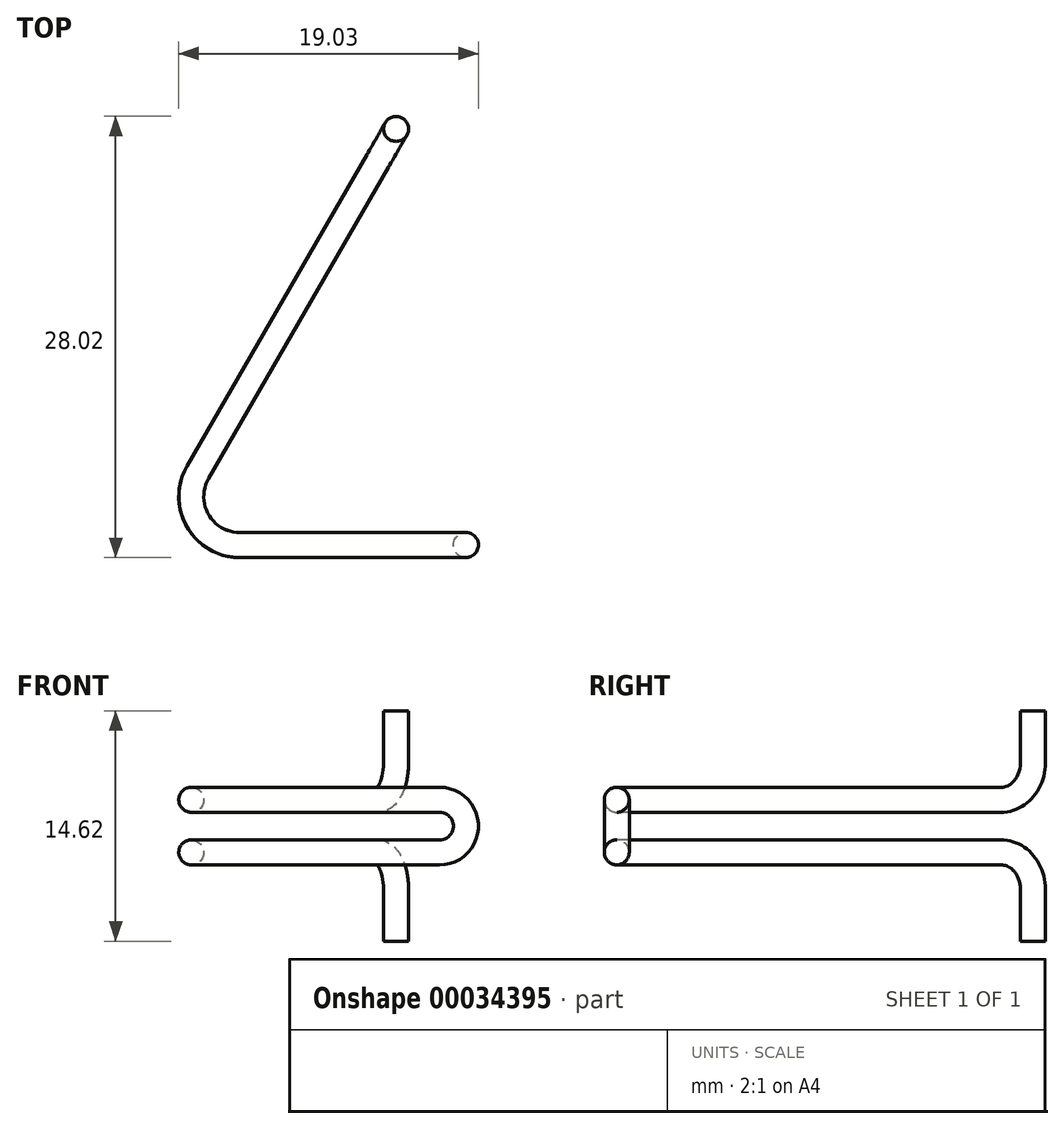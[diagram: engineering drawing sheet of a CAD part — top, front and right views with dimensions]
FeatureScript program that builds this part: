
annotation { "Feature Type Name" : "Feature", "Feature Type Description" : "" }
export const myFeature = defineFeature(function(context is Context, id is Id, definition is map)
    precondition{}
    {
        {
            var Q0;
            Q0=qCreatedBy(makeId("Top.planeOp"),FACE);
            var sketch = newSketch(context, id + "F0", { "sketchPlane" : qUnion([Q0])});
            skLineSegment(sketch, "E0", {"start": v(0, 0) * mm, "end": v(12.7, 0) * mm});
            skArc(sketch, "E1", {"start": v(-2.66, 4.61) * mm, "mid": v(-2.66, 1.54) * mm, "end": v(0, 0) * mm});
            skLineSegment(sketch, "E2", {"start": v(-2.66, 4.61) * mm, "end": v(8.77, 24.4) * mm});
            skSolve(sketch);
        }
        {
            var Q0;
            Q0=qCreatedBy(makeId("Right.planeOp"),FACE);
            var Q1;
            Q1=sQuery(id+"F0.wireOp",VERTEX,"E0.end");
            cPlane(context, id + "F1", {"entities" : qUnion([Q0, Q1]), "cplaneType" : CPlaneType.PLANE_POINT, "offset" : 152.4 * mm, "width" : 152.4 * mm, "height" : 152.4 * mm});
        }
        {
            var Q0;
            Q0=qCreatedBy(id+"F1.planeOp",FACE);
            var sketch = newSketch(context, id + "F2", { "sketchPlane" : qUnion([Q0])});
            skCircle(sketch, "E3", {"center": v(0, 0) * mm, "radius": 0.76 * mm});
            skSolve(sketch);
        }
        {
            var Q0;
            Q0=qCreatedBy(makeId("Front.planeOp"),FACE);
            var sketch = newSketch(context, id + "F3", { "sketchPlane" : qUnion([Q0])});
            skPoint(sketch, "E4.0", {"position": v(12.7, 0) * mm});
            skLineSegment(sketch, "E4.1", {"start": v(0, 0) * mm, "end": v(12.7, 0) * mm, "construction": true});
            skLineSegment(sketch, "E5", {"start": v(12.7, 0) * mm, "end": v(12.7, -3.34) * mm, "construction": true});
            skArc(sketch, "E6", {"start": v(12.7, -3.34) * mm, "mid": v(14.37, -1.67) * mm, "end": v(12.7, 0) * mm});
            skSolve(sketch);
        }
        {
            var Q0;
            Q0=qCreatedBy(makeId("Top.planeOp"),FACE);
            var Q1;
            Q1=sQuery(id+"F3.wireOp",VERTEX,"E6.start");
            cPlane(context, id + "F4", {"entities" : qUnion([Q0, Q1]), "cplaneType" : CPlaneType.PLANE_POINT, "offset" : 152.4 * mm, "width" : 152.4 * mm, "height" : 152.4 * mm});
        }
        {
            var Q0;
            Q0=qCreatedBy(id+"F4.planeOp",FACE);
            var sketch = newSketch(context, id + "F5", { "sketchPlane" : qUnion([Q0])});
            skLineSegment(sketch, "E7.0", {"start": v(0, 0) * mm, "end": v(12.7, 0) * mm});
            skArc(sketch, "E7.1", {"start": v(-2.66, 4.61) * mm, "mid": v(-2.66, 1.54) * mm, "end": v(0, 0) * mm});
            skLineSegment(sketch, "E7.2", {"start": v(-2.66, 4.61) * mm, "end": v(8.77, 24.4) * mm});
            skSolve(sketch);
        }
        {
            var Q0;
            Q0=sQuery(id+"F5.wireOp",EDGE,"E7.2");
            var Q1;
            Q1=sQuery(id+"F5.wireOp",VERTEX,"E7.2.end");
            cPlane(context, id + "F6", {"entities" : qUnion([Q0, Q1]), "cplaneType" : CPlaneType.LINE_POINT, "offset" : 152.4 * mm, "width" : 152.4 * mm, "height" : 152.4 * mm});
        }
        {
            var Q0;
            Q0=qCreatedBy(id+"F6.planeOp",FACE);
            var sketch = newSketch(context, id + "F7", { "sketchPlane" : qUnion([Q0])});
            skLineSegment(sketch, "E8.0", {"start": v(0, -3.34) * mm, "end": v(4.61, -3.34) * mm, "construction": true});
            skCircle(sketch, "E9", {"center": v(4.61, -3.34) * mm, "radius": 0.8 * mm});
            skSolve(sketch);
        }
        {
            var Q0;
            Q0=sQuery(id+"F7.wireOp",EDGE,"E8.0");
            var Q1;
            Q1=sQuery(id+"F5.wireOp",VERTEX,"E7.2.end");
            cPlane(context, id + "F8", {"entities" : qUnion([Q0, Q1]), "cplaneType" : CPlaneType.LINE_POINT, "offset" : 152.4 * mm, "width" : 152.4 * mm, "height" : 152.4 * mm});
        }
        {
            var Q0;
            Q0=qCreatedBy(id+"F8.planeOp",FACE);
            var sketch = newSketch(context, id + "F9", { "sketchPlane" : qUnion([Q0])});
            skLineSegment(sketch, "E10.0", {"start": v(-2.66, -3.34) * mm, "end": v(-25.52, -3.34) * mm, "construction": true});
            skLineSegment(sketch, "E11", {"start": v(-25.52, -3.34) * mm, "end": v(-25.52, -8.73) * mm, "construction": true});
            skArc(sketch, "E12", {"start": v(-25.52, -3.34) * mm, "mid": v(-27.17, -4.02) * mm, "end": v(-27.86, -5.68) * mm});
            skLineSegment(sketch, "E13", {"start": v(-25.52, -5.68) * mm, "end": v(-27.86, -5.68) * mm, "construction": true});
            skLineSegment(sketch, "E14", {"start": v(-27.86, -5.68) * mm, "end": v(-27.86, -8.98) * mm});
            skLineSegment(sketch, "E15.0", {"start": v(-2.66, 0) * mm, "end": v(-25.52, 0) * mm, "construction": true});
            skArc(sketch, "E16", {"start": v(-27.86, 2.34) * mm, "mid": v(-27.17, 0.68) * mm, "end": v(-25.52, 0) * mm});
            skLineSegment(sketch, "E17", {"start": v(-25.52, 0) * mm, "end": v(-25.52, 4.67) * mm, "construction": true});
            skLineSegment(sketch, "E18", {"start": v(-25.52, 2.34) * mm, "end": v(-27.86, 2.34) * mm});
            skLineSegment(sketch, "E19", {"start": v(-27.86, 2.34) * mm, "end": v(-27.86, 5.64) * mm});
            skSolve(sketch);
        }
        {
            var Q0;
            Q0=sQuery(id+"F9.wireOp",EDGE,"E14");
            var Q1;
            Q1=sQuery(id+"F9.wireOp",VERTEX,"E14.end");
            cPlane(context, id + "F10", {"entities" : qUnion([Q0, Q1]), "cplaneType" : CPlaneType.LINE_POINT, "offset" : 152.4 * mm, "width" : 152.4 * mm, "height" : 152.4 * mm});
        }
        {
            var Q0;
            Q0=qCreatedBy(id+"F10.planeOp",FACE);
            var sketch = newSketch(context, id + "F11", { "sketchPlane" : qUnion([Q0])});
            skLineSegment(sketch, "E20.0", {"start": v(8.77, -24.4) * mm, "end": v(9.94, -26.43) * mm, "construction": true});
            skCircle(sketch, "E21", {"center": v(9.94, -26.43) * mm, "radius": 0.8 * mm});
            skSolve(sketch);
        }
        {
            var Q0;
            Q0=makeQuery(id+"F11.imprint","IMPRINT",FACE,{"disambiguationData":[TD([[makeQuery(id+"F11.imprint","IMPRINT",EDGE,{"derivedFrom":sQuery(id+"F11.wireOp",EDGE,"E21")}),1.0]])]});
            var Q1;
            Q1=sQuery(id+"F9.wireOp",EDGE,"E14");
            var Q2;
            Q2=sQuery(id+"F9.wireOp",EDGE,"E12");
            var Q3;
            Q3=sQuery(id+"F5.wireOp",EDGE,"E7.2");
            var Q4;
            Q4=sQuery(id+"F5.wireOp",EDGE,"E7.1");
            var Q5;
            Q5=sQuery(id+"F5.wireOp",EDGE,"E7.0");
            var Q6;
            Q6=sQuery(id+"F3.wireOp",EDGE,"E6");
            var Q7;
            Q7=sQuery(id+"F0.wireOp",EDGE,"E0");
            var Q8;
            Q8=sQuery(id+"F0.wireOp",EDGE,"E1");
            var Q9;
            Q9=sQuery(id+"F0.wireOp",EDGE,"E2");
            var Q10;
            Q10=sQuery(id+"F9.wireOp",EDGE,"E16");
            var Q11;
            Q11=sQuery(id+"F9.wireOp",EDGE,"E19");
            sweep(context, id + "F12", {"profiles" : qUnion([Q0]), "path" : qUnion([Q1, Q2, Q3, Q4, Q5, Q6, Q7, Q8, Q9, Q10, Q11])});
        }
    });
